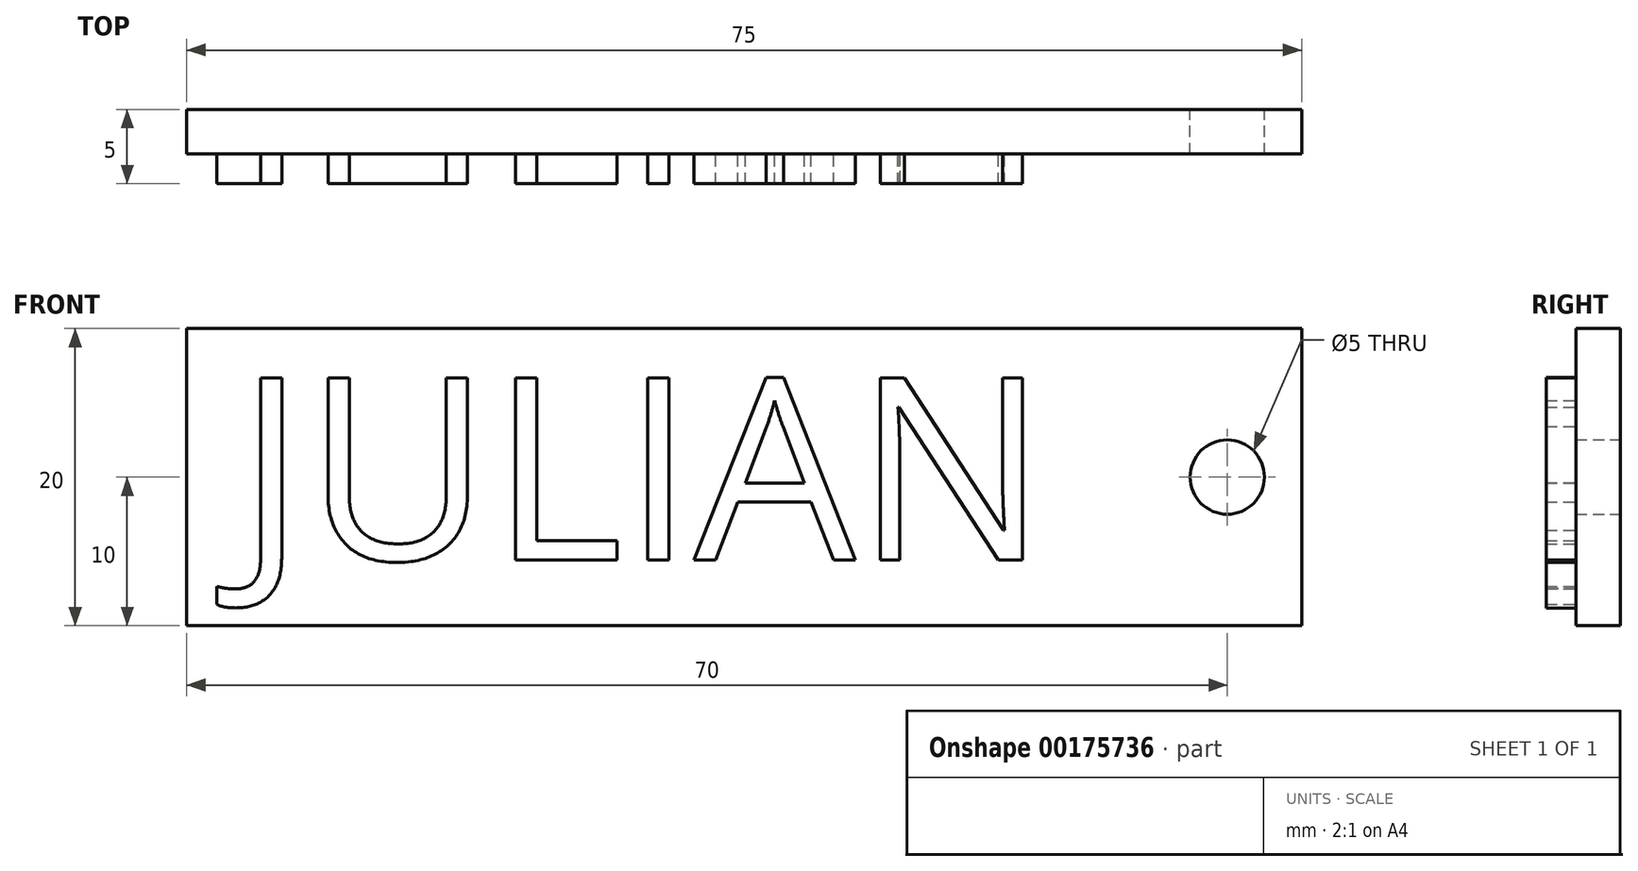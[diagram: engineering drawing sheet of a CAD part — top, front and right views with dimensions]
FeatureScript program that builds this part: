
annotation { "Feature Type Name" : "Feature", "Feature Type Description" : "" }
export const myFeature = defineFeature(function(context is Context, id is Id, definition is map)
    precondition{}
    {
        {
            var Q0;
            Q0=qCreatedBy(makeId("Front.planeOp"),FACE);
            var sketch = newSketch(context, id + "F0", { "sketchPlane" : qUnion([Q0])});
            skLineSegment(sketch, "E0.bottom", {"start": v(0, 0) * mm, "end": v(75, 0) * mm});
            skLineSegment(sketch, "E0.top", {"start": v(0, -20) * mm, "end": v(75, -20) * mm});
            skLineSegment(sketch, "E0.left", {"start": v(0, 0) * mm, "end": v(0, -20) * mm});
            skLineSegment(sketch, "E0.right", {"start": v(75, 0) * mm, "end": v(75, -20) * mm});
            skCircle(sketch, "E1", {"center": v(70, -10) * mm, "radius": 2.5 * mm});
            skSolve(sketch);
        }
        {
            var Q0;
            Q0 = qSketchRegion(id + "F0", true);
            extrude(context, id + "F1", {"entities" : qUnion([Q0]), "depth" : 3 * mm});
        }
        {
            var Q0;
            Q0=makeQuery(id+"F1.opExtrude","CAP_FACE",FACE,{"disambiguationData":[OSD([sQuery(id+"F0.wireOp",EDGE,"E0.bottom"),sQuery(id+"F0.wireOp",EDGE,"E0.top"),sQuery(id+"F0.wireOp",EDGE,"E0.left"),sQuery(id+"F0.wireOp",EDGE,"E0.right"),sQuery(id+"F0.wireOp",EDGE,"E1")])],"isStart":false});
            var sketch = newSketch(context, id + "F2", { "sketchPlane" : qUnion([Q0])});
            skText(sketch, "E2", { "text": "JULIAN", "fontName": "OpenSans-Regular.ttf"});
            const initialGuessF2  = {"E2": [0.00337, -0.01558, 1, 0, 0.01235]};
            skSetInitialGuess(sketch, initialGuessF2);
            skSolve(sketch);
        }
        {
            var Q0;
            Q0 = qSketchRegion(id + "F2", true);
            extrude(context, id + "F3", {"entities" : qUnion([Q0]), "operationType" : NewBodyOperationType.ADD, "depth" : 2 * mm});
        }
    });
